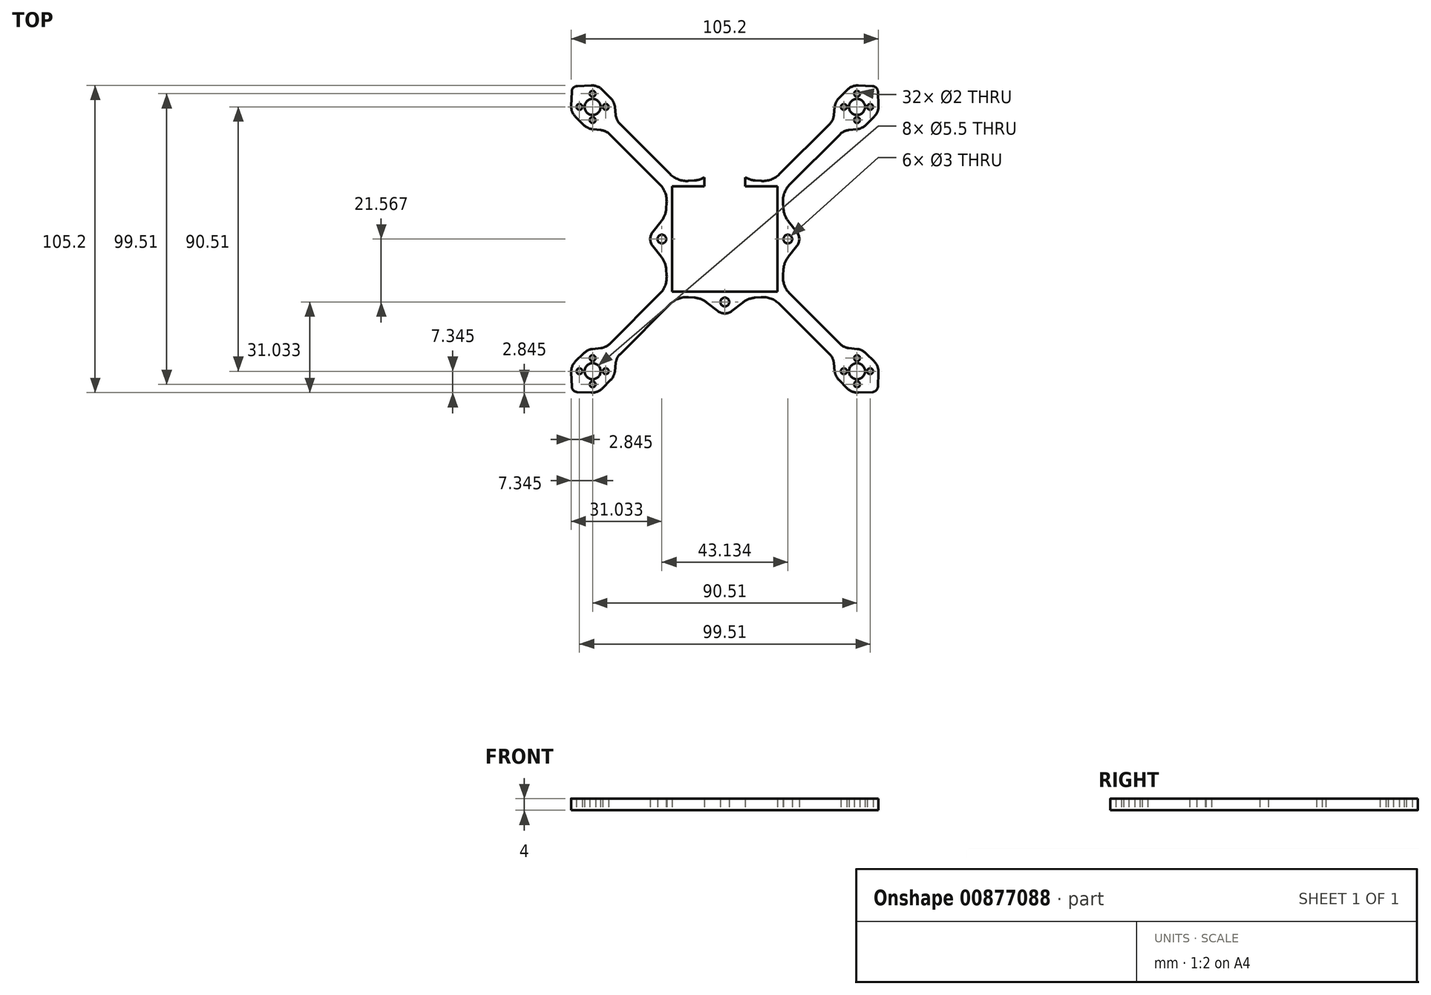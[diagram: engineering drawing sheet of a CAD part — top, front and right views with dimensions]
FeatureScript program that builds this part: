
annotation { "Feature Type Name" : "Feature", "Feature Type Description" : "" }
export const myFeature = defineFeature(function(context is Context, id is Id, definition is map)
    precondition{}
    {
        {
            var Q0;
            Q0=qCreatedBy(makeId("Top.planeOp"),FACE);
            var sketch = newSketch(context, id + "F0", { "sketchPlane" : qUnion([Q0])});
            skCircle(sketch, "E0", {"center": v(-45.25, 45.25) * mm, "radius": 44.45 * mm, "construction": true});
            skCircle(sketch, "E1", {"center": v(45.25, 45.25) * mm, "radius": 44.45 * mm, "construction": true});
            skCircle(sketch, "E2", {"center": v(45.25, -45.25) * mm, "radius": 44.45 * mm, "construction": true});
            skCircle(sketch, "E3", {"center": v(-45.25, -45.25) * mm, "radius": 44.45 * mm, "construction": true});
            skLineSegment(sketch, "E4.bottom", {"start": v(-45.25, 45.25) * mm, "end": v(45.25, 45.25) * mm, "construction": true});
            skLineSegment(sketch, "E4.top", {"start": v(-45.25, -45.25) * mm, "end": v(45.25, -45.25) * mm, "construction": true});
            skLineSegment(sketch, "E4.left", {"start": v(-45.25, 45.25) * mm, "end": v(-45.25, -45.25) * mm, "construction": true});
            skLineSegment(sketch, "E4.right", {"start": v(45.25, 45.25) * mm, "end": v(45.25, -45.25) * mm, "construction": true});
            skLineSegment(sketch, "E5", {"start": v(-45.25, -45.25) * mm, "end": v(45.25, 45.25) * mm, "construction": true});
            skLineSegment(sketch, "E6", {"start": v(45.25, -45.25) * mm, "end": v(-45.25, 45.25) * mm, "construction": true});
            skLineSegment(sketch, "E7", {"start": v(-27.65, 0) * mm, "end": v(0, 27.65) * mm, "construction": true});
            skLineSegment(sketch, "E8", {"start": v(0, 27.65) * mm, "end": v(27.65, 0) * mm, "construction": true});
            skLineSegment(sketch, "E9", {"start": v(27.65, 0) * mm, "end": v(0, -27.65) * mm, "construction": true});
            skLineSegment(sketch, "E10", {"start": v(0, -27.65) * mm, "end": v(-27.65, 0) * mm, "construction": true});
            skLineSegment(sketch, "E11.bottom", {"start": v(-18, 18) * mm, "end": v(18, 18) * mm});
            skLineSegment(sketch, "E11.top", {"start": v(-18, -18) * mm, "end": v(18, -18) * mm});
            skLineSegment(sketch, "E11.left", {"start": v(-18, 18) * mm, "end": v(-18, -18) * mm});
            skLineSegment(sketch, "E11.right", {"start": v(18, 18) * mm, "end": v(18, -18) * mm});
            skLineSegment(sketch, "E12.bottom", {"start": v(-15.25, 15.25) * mm, "end": v(15.25, 15.25) * mm, "construction": true});
            skLineSegment(sketch, "E12.top", {"start": v(-15.25, -15.25) * mm, "end": v(15.25, -15.25) * mm, "construction": true});
            skLineSegment(sketch, "E12.left", {"start": v(-15.25, 15.25) * mm, "end": v(-15.25, -15.25) * mm, "construction": true});
            skLineSegment(sketch, "E12.right", {"start": v(15.25, 15.25) * mm, "end": v(15.25, -15.25) * mm, "construction": true});
            skCircle(sketch, "E13.cCircle", {"center": v(45.25, -45.25) * mm, "radius": 4.5 * mm, "construction": true});
            skLineSegment(sketch, "E13.0", {"start": v(49.75, -45.25) * mm, "end": v(45.25, -49.75) * mm, "construction": true});
            skLineSegment(sketch, "E13.1", {"start": v(45.25, -49.75) * mm, "end": v(40.75, -45.25) * mm, "construction": true});
            skLineSegment(sketch, "E13.2", {"start": v(40.75, -45.25) * mm, "end": v(45.25, -40.75) * mm, "construction": true});
            skLineSegment(sketch, "E13.3", {"start": v(45.25, -40.75) * mm, "end": v(49.75, -45.25) * mm, "construction": true});
            skCircle(sketch, "E14", {"center": v(40.75, -45.25) * mm, "radius": 1 * mm});
            skCircle(sketch, "E15", {"center": v(45.25, -49.75) * mm, "radius": 1 * mm});
            skCircle(sketch, "E16", {"center": v(49.75, -45.25) * mm, "radius": 1 * mm});
            skCircle(sketch, "E17", {"center": v(45.25, -40.75) * mm, "radius": 1 * mm});
            skCircle(sketch, "E18", {"center": v(15.25, -15.25) * mm, "radius": 1.5 * mm});
            skLineSegment(sketch, "E19", {"start": v(18.7, -22.23) * mm, "end": v(35.88, -39.42) * mm});
            skLineSegment(sketch, "E20", {"start": v(37.32, -42.4) * mm, "end": v(37.64, -45.28) * mm});
            skLineSegment(sketch, "E21", {"start": v(39.07, -48.26) * mm, "end": v(41.94, -51.13) * mm});
            skLineSegment(sketch, "E22", {"start": v(45.67, -52.6) * mm, "end": v(50.48, -52.4) * mm});
            skLineSegment(sketch, "E23", {"start": v(45.25, -45.25) * mm, "end": v(40.66, -49.85) * mm, "construction": true});
            skPoint(sketch, "E24.endSnap0", {"position": v(0, -15.25) * mm});
            skLineSegment(sketch, "E25", {"start": v(6.09, -21.76) * mm, "end": v(0, -26.57) * mm});
            skPoint(sketch, "E26.visualSharp", {"position": v(37.12, -40.66) * mm});
            skArc(sketch, "E26.filletArc", {"start": v(37.32, -42.4) * mm, "mid": v(36.85, -40.79) * mm, "end": v(35.88, -39.42) * mm});
            skPoint(sketch, "E27.visualSharp", {"position": v(37.83, -47.02) * mm});
            skArc(sketch, "E27.filletArc", {"start": v(37.64, -45.28) * mm, "mid": v(38.1, -46.9) * mm, "end": v(39.07, -48.26) * mm});
            skPoint(sketch, "E28.visualSharp", {"position": v(43.49, -52.68) * mm});
            skArc(sketch, "E28.filletArc", {"start": v(41.94, -51.13) * mm, "mid": v(43.65, -52.25) * mm, "end": v(45.67, -52.6) * mm});
            skLineSegment(sketch, "E29", {"start": v(12.41, -19.9) * mm, "end": v(10.43, -20.06) * mm});
            skPoint(sketch, "E30.visualSharp", {"position": v(16.09, -19.62) * mm});
            skArc(sketch, "E30.filletArc", {"start": v(18.7, -22.23) * mm, "mid": v(15.8, -20.38) * mm, "end": v(12.41, -19.9) * mm});
            skPoint(sketch, "E31.visualSharp", {"position": v(8, -20.25) * mm});
            skArc(sketch, "E31.filletArc", {"start": v(10.43, -20.06) * mm, "mid": v(8.13, -20.59) * mm, "end": v(6.09, -21.76) * mm});
            skLineSegment(sketch, "E32.MirrorCS", {"start": v(21.76, -6.09) * mm, "end": v(26.57, 0) * mm});
            skArc(sketch, "E33.MirrorCS", {"start": v(20.06, -10.43) * mm, "mid": v(20.59, -8.13) * mm, "end": v(21.76, -6.09) * mm});
            skPoint(sketch, "E34.MirrorP", {"position": v(20.25, -8) * mm});
            skPoint(sketch, "E35.MirrorP", {"position": v(19.62, -16.09) * mm});
            skLineSegment(sketch, "E36.MirrorCS", {"start": v(19.9, -12.41) * mm, "end": v(20.06, -10.43) * mm});
            skArc(sketch, "E37.MirrorCS", {"start": v(22.23, -18.7) * mm, "mid": v(20.38, -15.8) * mm, "end": v(19.9, -12.41) * mm});
            skLineSegment(sketch, "E38.MirrorCS", {"start": v(22.23, -18.7) * mm, "end": v(39.42, -35.88) * mm});
            skPoint(sketch, "E39.MirrorP", {"position": v(40.66, -37.12) * mm});
            skArc(sketch, "E40.MirrorCS", {"start": v(42.4, -37.32) * mm, "mid": v(40.79, -36.85) * mm, "end": v(39.42, -35.88) * mm});
            skLineSegment(sketch, "E41.MirrorCS", {"start": v(42.4, -37.32) * mm, "end": v(45.28, -37.64) * mm});
            skPoint(sketch, "E42.MirrorP", {"position": v(47.02, -37.83) * mm});
            skArc(sketch, "E43.MirrorCS", {"start": v(45.28, -37.64) * mm, "mid": v(46.9, -38.1) * mm, "end": v(48.26, -39.07) * mm});
            skLineSegment(sketch, "E44.MirrorCS", {"start": v(52.6, -45.67) * mm, "end": v(52.4, -50.48) * mm});
            skLineSegment(sketch, "E45.MirrorCS", {"start": v(48.26, -39.07) * mm, "end": v(51.13, -41.94) * mm});
            skPoint(sketch, "E46.MirrorP", {"position": v(52.68, -43.49) * mm});
            skArc(sketch, "E47.MirrorCS", {"start": v(51.13, -41.94) * mm, "mid": v(52.25, -43.65) * mm, "end": v(52.6, -45.67) * mm});
            skPoint(sketch, "E48.visualSharp", {"position": v(52.33, -52.33) * mm});
            skArc(sketch, "E48.filletArc", {"start": v(50.48, -52.4) * mm, "mid": v(51.82, -51.82) * mm, "end": v(52.4, -50.48) * mm});
            skArc(sketch, "E49.MirrorCS", {"start": v(20.06, 10.43) * mm, "mid": v(20.59, 8.13) * mm, "end": v(21.76, 6.09) * mm});
            skPoint(sketch, "E50.MirrorP", {"position": v(20.25, 8) * mm});
            skLineSegment(sketch, "E51.MirrorCS", {"start": v(21.76, 6.09) * mm, "end": v(26.57, 0) * mm});
            skLineSegment(sketch, "E52.MirrorCS", {"start": v(19.9, 12.41) * mm, "end": v(20.06, 10.43) * mm});
            skArc(sketch, "E53.MirrorCS", {"start": v(22.23, 18.7) * mm, "mid": v(20.38, 15.8) * mm, "end": v(19.9, 12.41) * mm});
            skPoint(sketch, "E54.MirrorP", {"position": v(19.62, 16.09) * mm});
            skLineSegment(sketch, "E55.MirrorCS", {"start": v(22.23, 18.7) * mm, "end": v(39.42, 35.88) * mm});
            skArc(sketch, "E56.MirrorCS", {"start": v(42.4, 37.32) * mm, "mid": v(40.79, 36.85) * mm, "end": v(39.42, 35.88) * mm});
            skArc(sketch, "E57.MirrorCS", {"start": v(45.28, 37.64) * mm, "mid": v(46.9, 38.1) * mm, "end": v(48.26, 39.07) * mm});
            skPoint(sketch, "E58.MirrorP", {"position": v(40.66, 37.12) * mm});
            skLineSegment(sketch, "E59.MirrorCS", {"start": v(42.4, 37.32) * mm, "end": v(45.28, 37.64) * mm});
            skPoint(sketch, "E60.MirrorP", {"position": v(47.02, 37.83) * mm});
            skCircle(sketch, "E61.MirrorC", {"center": v(45.25, 40.75) * mm, "radius": 1 * mm});
            skLineSegment(sketch, "E62.MirrorCS", {"start": v(48.26, 39.07) * mm, "end": v(51.13, 41.94) * mm});
            skCircle(sketch, "E63.MirrorC", {"center": v(49.75, 45.25) * mm, "radius": 1 * mm});
            skCircle(sketch, "E64.MirrorC", {"center": v(45.25, 45.25) * mm, "radius": 4.5 * mm, "construction": true});
            skLineSegment(sketch, "E65.MirrorCS", {"start": v(40.75, 45.25) * mm, "end": v(45.25, 40.75) * mm, "construction": true});
            skArc(sketch, "E66.MirrorCS", {"start": v(51.13, 41.94) * mm, "mid": v(52.25, 43.65) * mm, "end": v(52.6, 45.67) * mm});
            skPoint(sketch, "E67.MirrorP", {"position": v(52.68, 43.49) * mm});
            skLineSegment(sketch, "E68.MirrorCS", {"start": v(52.6, 45.67) * mm, "end": v(52.4, 50.48) * mm});
            skCircle(sketch, "E69.MirrorC", {"center": v(45.25, 49.75) * mm, "radius": 1 * mm});
            skLineSegment(sketch, "E70.MirrorCS", {"start": v(45.25, 40.75) * mm, "end": v(49.75, 45.25) * mm, "construction": true});
            skLineSegment(sketch, "E71.MirrorCS", {"start": v(49.75, 45.25) * mm, "end": v(45.25, 49.75) * mm, "construction": true});
            skArc(sketch, "E72.MirrorCS", {"start": v(50.48, 52.4) * mm, "mid": v(51.82, 51.82) * mm, "end": v(52.4, 50.48) * mm});
            skLineSegment(sketch, "E73.MirrorCS", {"start": v(45.67, 52.6) * mm, "end": v(50.48, 52.4) * mm});
            skPoint(sketch, "E74.MirrorP", {"position": v(52.33, 52.33) * mm});
            skArc(sketch, "E75.MirrorCS", {"start": v(37.64, 45.28) * mm, "mid": v(38.1, 46.9) * mm, "end": v(39.07, 48.26) * mm});
            skLineSegment(sketch, "E76.MirrorCS", {"start": v(39.07, 48.26) * mm, "end": v(41.94, 51.13) * mm});
            skArc(sketch, "E77.MirrorCS", {"start": v(41.94, 51.13) * mm, "mid": v(43.65, 52.25) * mm, "end": v(45.67, 52.6) * mm});
            skLineSegment(sketch, "E78.MirrorCS", {"start": v(45.25, 45.25) * mm, "end": v(40.66, 49.85) * mm, "construction": true});
            skLineSegment(sketch, "E79.MirrorCS", {"start": v(45.25, 49.75) * mm, "end": v(40.75, 45.25) * mm, "construction": true});
            skCircle(sketch, "E80.MirrorC", {"center": v(40.75, 45.25) * mm, "radius": 1 * mm});
            skPoint(sketch, "E81.MirrorP", {"position": v(43.49, 52.68) * mm});
            skPoint(sketch, "E82.MirrorP", {"position": v(37.83, 47.02) * mm});
            skLineSegment(sketch, "E83.MirrorCS", {"start": v(37.32, 42.4) * mm, "end": v(37.64, 45.28) * mm});
            skArc(sketch, "E84.MirrorCS", {"start": v(37.32, 42.4) * mm, "mid": v(36.85, 40.79) * mm, "end": v(35.88, 39.42) * mm});
            skLineSegment(sketch, "E85.MirrorCS", {"start": v(18.7, 22.23) * mm, "end": v(35.88, 39.42) * mm});
            skPoint(sketch, "E86.MirrorP", {"position": v(37.12, 40.66) * mm});
            skArc(sketch, "E87.MirrorCS", {"start": v(18.7, 22.23) * mm, "mid": v(15.8, 20.38) * mm, "end": v(12.41, 19.9) * mm});
            skPoint(sketch, "E88.MirrorP", {"position": v(16.09, 19.62) * mm});
            skLineSegment(sketch, "E89.MirrorCS", {"start": v(12.41, 19.9) * mm, "end": v(10.43, 20.06) * mm});
            skPoint(sketch, "E90.MirrorP", {"position": v(8, 20.25) * mm});
            skArc(sketch, "E91.MirrorCS", {"start": v(10.43, 20.06) * mm, "mid": v(8.13, 20.59) * mm, "end": v(6.09, 21.76) * mm});
            skLineSegment(sketch, "E92.MirrorCS", {"start": v(6.09, 21.76) * mm, "end": v(0, 26.57) * mm});
            skArc(sketch, "E93.MirrorCS", {"start": v(-10.43, -20.06) * mm, "mid": v(-8.13, -20.59) * mm, "end": v(-6.09, -21.76) * mm});
            skPoint(sketch, "E94.MirrorP", {"position": v(-8, -20.25) * mm});
            skLineSegment(sketch, "E95.MirrorCS", {"start": v(-6.09, -21.76) * mm, "end": v(0, -26.57) * mm});
            skLineSegment(sketch, "E96.MirrorCS", {"start": v(-12.41, -19.9) * mm, "end": v(-10.43, -20.06) * mm});
            skArc(sketch, "E97.MirrorCS", {"start": v(-18.7, -22.23) * mm, "mid": v(-15.8, -20.38) * mm, "end": v(-12.41, -19.9) * mm});
            skPoint(sketch, "E98.MirrorP", {"position": v(-16.09, -19.62) * mm});
            skLineSegment(sketch, "E99.MirrorCS", {"start": v(-18.7, -22.23) * mm, "end": v(-35.88, -39.42) * mm});
            skArc(sketch, "E100.MirrorCS", {"start": v(-45.28, -37.64) * mm, "mid": v(-46.9, -38.1) * mm, "end": v(-48.26, -39.07) * mm});
            skArc(sketch, "E101.MirrorCS", {"start": v(-37.32, -42.4) * mm, "mid": v(-36.85, -40.79) * mm, "end": v(-35.88, -39.42) * mm});
            skArc(sketch, "E102.MirrorCS", {"start": v(-42.4, -37.32) * mm, "mid": v(-40.79, -36.85) * mm, "end": v(-39.42, -35.88) * mm});
            skArc(sketch, "E103.MirrorCS", {"start": v(-37.64, -45.28) * mm, "mid": v(-38.1, -46.9) * mm, "end": v(-39.07, -48.26) * mm});
            skPoint(sketch, "E104.MirrorP", {"position": v(-40.66, -37.12) * mm});
            skCircle(sketch, "E105.MirrorC", {"center": v(-40.75, -45.25) * mm, "radius": 1 * mm});
            skPoint(sketch, "E106.MirrorP", {"position": v(-47.02, -37.83) * mm});
            skLineSegment(sketch, "E107.MirrorCS", {"start": v(-37.32, -42.4) * mm, "end": v(-37.64, -45.28) * mm});
            skCircle(sketch, "E108.MirrorC", {"center": v(-45.25, -45.25) * mm, "radius": 4.5 * mm, "construction": true});
            skLineSegment(sketch, "E109.MirrorCS", {"start": v(-48.26, -39.07) * mm, "end": v(-51.13, -41.94) * mm});
            skLineSegment(sketch, "E110.MirrorCS", {"start": v(-45.25, -45.25) * mm, "end": v(-40.66, -49.85) * mm, "construction": true});
            skLineSegment(sketch, "E111.MirrorCS", {"start": v(-22.23, -18.7) * mm, "end": v(-39.42, -35.88) * mm});
            skPoint(sketch, "E112.MirrorP", {"position": v(-37.83, -47.02) * mm});
            skPoint(sketch, "E113.MirrorP", {"position": v(-37.12, -40.66) * mm});
            skArc(sketch, "E114.MirrorCS", {"start": v(-51.13, -41.94) * mm, "mid": v(-52.25, -43.65) * mm, "end": v(-52.6, -45.67) * mm});
            skPoint(sketch, "E115.MirrorP", {"position": v(-43.49, -52.68) * mm});
            skPoint(sketch, "E116.MirrorP", {"position": v(-52.68, -43.49) * mm});
            skLineSegment(sketch, "E117.MirrorCS", {"start": v(-40.75, -45.25) * mm, "end": v(-45.25, -40.75) * mm, "construction": true});
            skCircle(sketch, "E118.MirrorC", {"center": v(-45.25, -40.75) * mm, "radius": 1 * mm});
            skArc(sketch, "E119.MirrorCS", {"start": v(-50.48, -52.4) * mm, "mid": v(-51.82, -51.82) * mm, "end": v(-52.4, -50.48) * mm});
            skLineSegment(sketch, "E120.MirrorCS", {"start": v(-52.6, -45.67) * mm, "end": v(-52.4, -50.48) * mm});
            skLineSegment(sketch, "E121.MirrorCS", {"start": v(-45.25, -49.75) * mm, "end": v(-40.75, -45.25) * mm, "construction": true});
            skLineSegment(sketch, "E122.MirrorCS", {"start": v(-49.75, -45.25) * mm, "end": v(-45.25, -49.75) * mm, "construction": true});
            skLineSegment(sketch, "E123.MirrorCS", {"start": v(-42.4, -37.32) * mm, "end": v(-45.28, -37.64) * mm});
            skCircle(sketch, "E124.MirrorC", {"center": v(-49.75, -45.25) * mm, "radius": 1 * mm});
            skArc(sketch, "E125.MirrorCS", {"start": v(-41.94, -51.13) * mm, "mid": v(-43.65, -52.25) * mm, "end": v(-45.67, -52.6) * mm});
            skCircle(sketch, "E126.MirrorC", {"center": v(-45.25, -49.75) * mm, "radius": 1 * mm});
            skLineSegment(sketch, "E127.MirrorCS", {"start": v(-45.25, -40.75) * mm, "end": v(-49.75, -45.25) * mm, "construction": true});
            skLineSegment(sketch, "E128.MirrorCS", {"start": v(-39.07, -48.26) * mm, "end": v(-41.94, -51.13) * mm});
            skLineSegment(sketch, "E129.MirrorCS", {"start": v(-45.67, -52.6) * mm, "end": v(-50.48, -52.4) * mm});
            skPoint(sketch, "E130.MirrorP", {"position": v(-52.33, -52.33) * mm});
            skPoint(sketch, "E131.MirrorP", {"position": v(-19.62, -16.09) * mm});
            skLineSegment(sketch, "E132.MirrorCS", {"start": v(-19.9, -12.41) * mm, "end": v(-20.06, -10.43) * mm});
            skArc(sketch, "E133.MirrorCS", {"start": v(-22.23, -18.7) * mm, "mid": v(-20.38, -15.8) * mm, "end": v(-19.9, -12.41) * mm});
            skArc(sketch, "E134.MirrorCS", {"start": v(-20.06, 10.43) * mm, "mid": v(-20.59, 8.13) * mm, "end": v(-21.76, 6.09) * mm});
            skArc(sketch, "E135.MirrorCS", {"start": v(-20.06, -10.43) * mm, "mid": v(-20.59, -8.13) * mm, "end": v(-21.76, -6.09) * mm});
            skLineSegment(sketch, "E136.MirrorCS", {"start": v(-19.9, 12.41) * mm, "end": v(-20.06, 10.43) * mm});
            skLineSegment(sketch, "E137.MirrorCS", {"start": v(-21.76, 6.09) * mm, "end": v(-26.57, 0) * mm});
            skPoint(sketch, "E138.MirrorP", {"position": v(-20.25, -8) * mm});
            skLineSegment(sketch, "E139.MirrorCS", {"start": v(-21.76, -6.09) * mm, "end": v(-26.57, 0) * mm});
            skPoint(sketch, "E140.MirrorP", {"position": v(-20.25, 8) * mm});
            skPoint(sketch, "E141.MirrorP", {"position": v(-19.62, 16.09) * mm});
            skLineSegment(sketch, "E142.MirrorCS", {"start": v(-22.23, 18.7) * mm, "end": v(-39.42, 35.88) * mm});
            skArc(sketch, "E143.MirrorCS", {"start": v(-22.23, 18.7) * mm, "mid": v(-20.38, 15.8) * mm, "end": v(-19.9, 12.41) * mm});
            skArc(sketch, "E144.MirrorCS", {"start": v(-37.64, 45.28) * mm, "mid": v(-38.1, 46.9) * mm, "end": v(-39.07, 48.26) * mm});
            skPoint(sketch, "E145.MirrorP", {"position": v(-43.49, 52.68) * mm});
            skLineSegment(sketch, "E146.MirrorCS", {"start": v(-45.67, 52.6) * mm, "end": v(-50.48, 52.4) * mm});
            skPoint(sketch, "E147.MirrorP", {"position": v(-52.68, 43.49) * mm});
            skLineSegment(sketch, "E148.MirrorCS", {"start": v(-39.07, 48.26) * mm, "end": v(-41.94, 51.13) * mm});
            skLineSegment(sketch, "E149.MirrorCS", {"start": v(-52.6, 45.67) * mm, "end": v(-52.4, 50.48) * mm});
            skPoint(sketch, "E150.MirrorP", {"position": v(-37.83, 47.02) * mm});
            skLineSegment(sketch, "E151.MirrorCS", {"start": v(-37.32, 42.4) * mm, "end": v(-37.64, 45.28) * mm});
            skLineSegment(sketch, "E152.MirrorCS", {"start": v(-49.75, 45.25) * mm, "end": v(-45.25, 49.75) * mm, "construction": true});
            skCircle(sketch, "E153.MirrorC", {"center": v(-45.25, 49.75) * mm, "radius": 1 * mm});
            skArc(sketch, "E154.MirrorCS", {"start": v(-41.94, 51.13) * mm, "mid": v(-43.65, 52.25) * mm, "end": v(-45.67, 52.6) * mm});
            skArc(sketch, "E155.MirrorCS", {"start": v(-51.13, 41.94) * mm, "mid": v(-52.25, 43.65) * mm, "end": v(-52.6, 45.67) * mm});
            skLineSegment(sketch, "E156.MirrorCS", {"start": v(-45.25, 45.25) * mm, "end": v(-40.66, 49.85) * mm, "construction": true});
            skLineSegment(sketch, "E157.MirrorCS", {"start": v(-45.25, 40.75) * mm, "end": v(-49.75, 45.25) * mm, "construction": true});
            skArc(sketch, "E158.MirrorCS", {"start": v(-50.48, 52.4) * mm, "mid": v(-51.82, 51.82) * mm, "end": v(-52.4, 50.48) * mm});
            skLineSegment(sketch, "E159.MirrorCS", {"start": v(-40.75, 45.25) * mm, "end": v(-45.25, 40.75) * mm, "construction": true});
            skLineSegment(sketch, "E160.MirrorCS", {"start": v(-45.25, 49.75) * mm, "end": v(-40.75, 45.25) * mm, "construction": true});
            skCircle(sketch, "E161.MirrorC", {"center": v(-45.25, 45.25) * mm, "radius": 4.5 * mm, "construction": true});
            skCircle(sketch, "E162.MirrorC", {"center": v(-49.75, 45.25) * mm, "radius": 1 * mm});
            skPoint(sketch, "E163.MirrorP", {"position": v(-52.33, 52.33) * mm});
            skCircle(sketch, "E164.MirrorC", {"center": v(-40.75, 45.25) * mm, "radius": 1 * mm});
            skArc(sketch, "E165.MirrorCS", {"start": v(-42.4, 37.32) * mm, "mid": v(-40.79, 36.85) * mm, "end": v(-39.42, 35.88) * mm});
            skArc(sketch, "E166.MirrorCS", {"start": v(-37.32, 42.4) * mm, "mid": v(-36.85, 40.79) * mm, "end": v(-35.88, 39.42) * mm});
            skArc(sketch, "E167.MirrorCS", {"start": v(-45.28, 37.64) * mm, "mid": v(-46.9, 38.1) * mm, "end": v(-48.26, 39.07) * mm});
            skPoint(sketch, "E168.MirrorP", {"position": v(-37.12, 40.66) * mm});
            skCircle(sketch, "E169.MirrorC", {"center": v(-45.25, 40.75) * mm, "radius": 1 * mm});
            skLineSegment(sketch, "E170.MirrorCS", {"start": v(-18.7, 22.23) * mm, "end": v(-35.88, 39.42) * mm});
            skLineSegment(sketch, "E171.MirrorCS", {"start": v(-48.26, 39.07) * mm, "end": v(-51.13, 41.94) * mm});
            skLineSegment(sketch, "E172.MirrorCS", {"start": v(-42.4, 37.32) * mm, "end": v(-45.28, 37.64) * mm});
            skPoint(sketch, "E173.MirrorP", {"position": v(-40.66, 37.12) * mm});
            skPoint(sketch, "E174.MirrorP", {"position": v(-47.02, 37.83) * mm});
            skArc(sketch, "E175.MirrorCS", {"start": v(-10.43, 20.06) * mm, "mid": v(-8.13, 20.59) * mm, "end": v(-6.09, 21.76) * mm});
            skPoint(sketch, "E176.MirrorP", {"position": v(-16.09, 19.62) * mm});
            skPoint(sketch, "E177.MirrorP", {"position": v(-8, 20.25) * mm});
            skLineSegment(sketch, "E178.MirrorCS", {"start": v(-6.09, 21.76) * mm, "end": v(0, 26.57) * mm});
            skArc(sketch, "E179.MirrorCS", {"start": v(-18.7, 22.23) * mm, "mid": v(-15.8, 20.38) * mm, "end": v(-12.41, 19.9) * mm});
            skLineSegment(sketch, "E180.MirrorCS", {"start": v(-12.41, 19.9) * mm, "end": v(-10.43, 20.06) * mm});
            skCircle(sketch, "E181", {"center": v(-15.25, 15.25) * mm, "radius": 1.5 * mm});
            skCircle(sketch, "E182", {"center": v(-15.25, -15.25) * mm, "radius": 1.5 * mm});
            skCircle(sketch, "E183", {"center": v(15.25, 15.25) * mm, "radius": 1.5 * mm});
            skLineSegment(sketch, "E184", {"start": v(-21.57, 0) * mm, "end": v(0, 21.57) * mm, "construction": true});
            skPoint(sketch, "E184.endSnap0", {"position": v(0, 15.25) * mm});
            skLineSegment(sketch, "E185", {"start": v(0, 21.57) * mm, "end": v(21.57, 0) * mm, "construction": true});
            skLineSegment(sketch, "E186", {"start": v(21.57, 0) * mm, "end": v(0, -21.57) * mm, "construction": true});
            skLineSegment(sketch, "E187", {"start": v(0, -21.57) * mm, "end": v(-21.57, 0) * mm, "construction": true});
            skCircle(sketch, "E188", {"center": v(0, -21.57) * mm, "radius": 1.5 * mm});
            skCircle(sketch, "E189", {"center": v(21.57, 0) * mm, "radius": 1.5 * mm});
            skCircle(sketch, "E190", {"center": v(0, 21.57) * mm, "radius": 1.5 * mm});
            skCircle(sketch, "E191", {"center": v(-21.57, 0) * mm, "radius": 1.5 * mm});
            skArc(sketch, "E192", {"start": v(-2.43, -24.65) * mm, "mid": v(0, -25.5) * mm, "end": v(2.43, -24.65) * mm});
            skArc(sketch, "E193", {"start": v(24.65, -2.43) * mm, "mid": v(25.5, 0) * mm, "end": v(24.65, 2.43) * mm});
            skArc(sketch, "E194", {"start": v(-24.65, 2.43) * mm, "mid": v(-25.5, 0) * mm, "end": v(-24.65, -2.43) * mm});
            skLineSegment(sketch, "E195.bottom", {"start": v(-10, 10) * mm, "end": v(10, 10) * mm, "construction": true});
            skLineSegment(sketch, "E195.top", {"start": v(-10, -10) * mm, "end": v(10, -10) * mm, "construction": true});
            skLineSegment(sketch, "E195.left", {"start": v(-10, 10) * mm, "end": v(-10, -10) * mm, "construction": true});
            skLineSegment(sketch, "E195.right", {"start": v(10, 10) * mm, "end": v(10, -10) * mm, "construction": true});
            skCircle(sketch, "E196", {"center": v(-10, -10) * mm, "radius": 1 * mm});
            skCircle(sketch, "E197", {"center": v(10, -10) * mm, "radius": 1 * mm});
            skCircle(sketch, "E198", {"center": v(10, 10) * mm, "radius": 1 * mm});
            skCircle(sketch, "E199", {"center": v(-10, 10) * mm, "radius": 1 * mm});
            skCircle(sketch, "E200", {"center": v(0, 0) * mm, "radius": 10 * mm});
            skCircle(sketch, "E201", {"center": v(45.25, -45.25) * mm, "radius": 2.75 * mm});
            skCircle(sketch, "E202", {"center": v(45.25, 45.25) * mm, "radius": 2.75 * mm});
            skCircle(sketch, "E203", {"center": v(-45.25, 45.25) * mm, "radius": 2.75 * mm});
            skCircle(sketch, "E204", {"center": v(-45.25, -45.25) * mm, "radius": 2.75 * mm});
            skLineSegment(sketch, "E205", {"start": v(-7, 18) * mm, "end": v(-7, 33) * mm});
            skLineSegment(sketch, "E206", {"start": v(-7, 33) * mm, "end": v(7, 33) * mm});
            skLineSegment(sketch, "E207", {"start": v(7, 33) * mm, "end": v(7, 18) * mm});
            skLineSegment(sketch, "E208", {"start": v(-11, -16.93) * mm, "end": v(11, -16.93) * mm, "construction": true});
            skSolve(sketch);
        }
        {
            var Q0;
            Q0=makeQuery(id+"F0.imprint","IMPRINT",FACE,{"disambiguationData":[TD([[makeQuery(id+"F0.imprint","IMPRINT",EDGE,{"derivedFrom":sQuery(id+"F0.wireOp",EDGE,"E14")}),-1.0]])]});
            extrude(context, id + "F1", {"entities" : qUnion([Q0]), "depth" : 4 * mm, "offsetDistance" : 25 * mm});
        }
    });
